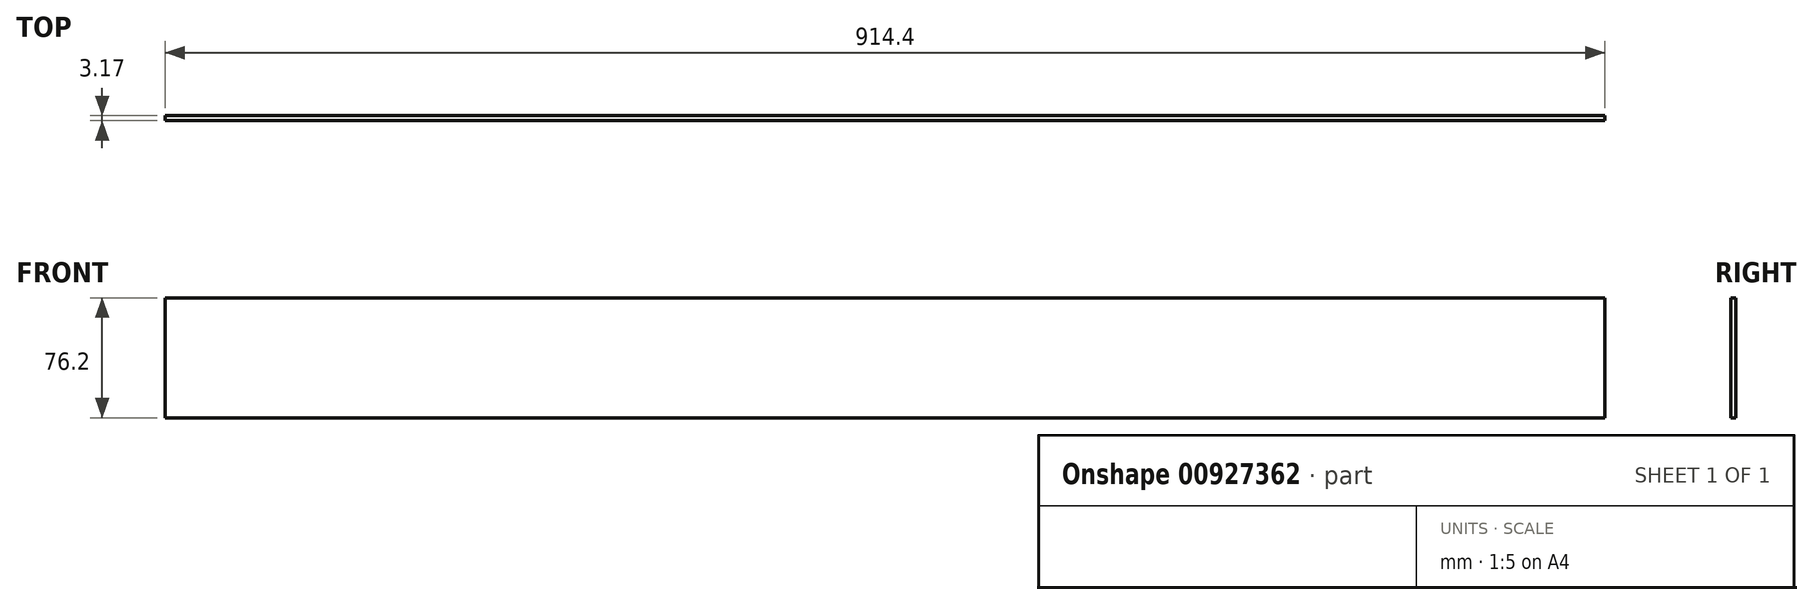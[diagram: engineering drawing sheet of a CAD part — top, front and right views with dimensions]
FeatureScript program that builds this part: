
annotation { "Feature Type Name" : "Feature", "Feature Type Description" : "" }
export const myFeature = defineFeature(function(context is Context, id is Id, definition is map)
    precondition{}
    {
        {
            var Q0;
            Q0=qCreatedBy(makeId("Front.planeOp"),FACE);
            var sketch = newSketch(context, id + "F0", { "sketchPlane" : qUnion([Q0])});
            skLineSegment(sketch, "E0.bottom", {"start": v(457.2, 38.1) * mm, "end": v(-457.2, 38.1) * mm});
            skLineSegment(sketch, "E0.top", {"start": v(457.2, -38.1) * mm, "end": v(-457.2, -38.1) * mm});
            skLineSegment(sketch, "E0.left", {"start": v(457.2, 38.1) * mm, "end": v(457.2, -38.1) * mm});
            skLineSegment(sketch, "E0.right", {"start": v(-457.2, 38.1) * mm, "end": v(-457.2, -38.1) * mm});
            skPoint(sketch, "E0.middle", {"position": v(0, 0) * mm});
            skSolve(sketch);
        }
        {
            var Q0;
            Q0=makeQuery(id+"F0.imprint","IMPRINT",FACE,{"disambiguationData":[TD([[makeQuery(id+"F0.imprint","IMPRINT",EDGE,{"derivedFrom":sQuery(id+"F0.wireOp",EDGE,"E0.bottom")}),1.0]])]});
            extrude(context, id + "F1", {"entities" : qUnion([Q0]), "depth" : 3.17 * mm, "offsetDistance" : 25.4 * mm});
        }
    });
